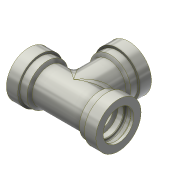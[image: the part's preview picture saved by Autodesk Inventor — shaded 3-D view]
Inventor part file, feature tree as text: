
AUTODESK INVENTOR PART (.ipt)
format: ipt  version: 2021 (Build 250183000, 183)  size: 372,224 bytes
history: native  units: mm
features: other x4, sketch x4, revolve x2, hole x2, fillet x1, projected_geometry x1
ambient origin geometry x8: Origin, YZ Plane, XZ Plane, XY Plane, X Axis, Y Axis, Z Axis, Center Point
bodies: Body1 (feature_tree)
feature tree (14):
  other  "Твердое тело1"
  revolve  "Вращение1"
  other  "РабПлоскость2"
  revolve  "Вращение2"
  hole  "Отверстие1"  [1 undecoded]
  hole  "Отверстие2"  [1 undecoded]
  fillet  "Сопряжение1"  Radius=7.0mm
  other  "РабПлоскость3"
  other  "РабПлоскость4"
  sketch  "Эскиз1"
  sketch  "Эскиз3"
  sketch  "Эскиз4"
  sketch  "Эскиз6"
  projected_geometry  "Спроецированная петля1"
note: 2 required parameter values undecoded (feature->parameter linkage not recoverable at this tier; creation-order binding heuristic only, values carry confidence <= 0.55)
